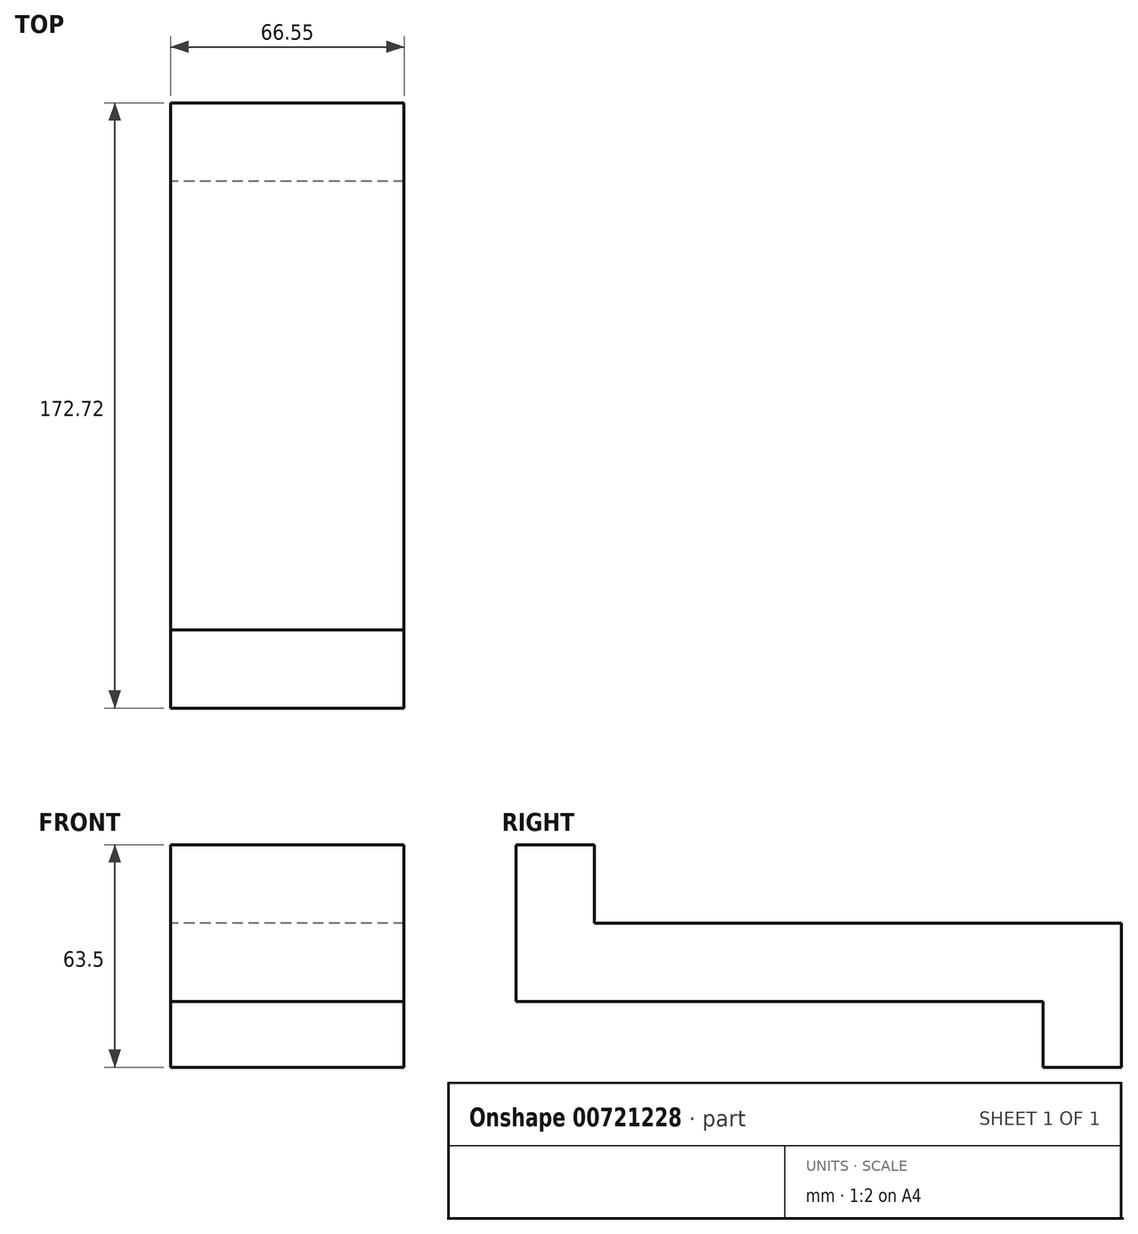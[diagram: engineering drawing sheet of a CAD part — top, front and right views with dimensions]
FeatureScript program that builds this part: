
annotation { "Feature Type Name" : "Feature", "Feature Type Description" : "" }
export const myFeature = defineFeature(function(context is Context, id is Id, definition is map)
    precondition{}
    {
        {
            var Q0;
            Q0=qCreatedBy(makeId("Right.planeOp"),FACE);
            var sketch = newSketch(context, id + "F0", { "sketchPlane" : qUnion([Q0])});
            skLineSegment(sketch, "E0.bottom", {"start": v(-92.13, 44.7) * mm, "end": v(-69.78, 44.7) * mm});
            skLineSegment(sketch, "E0.right", {"start": v(-69.78, 44.7) * mm, "end": v(-69.78, 22.35) * mm});
            skLineSegment(sketch, "E1.bottom", {"start": v(-69.78, 22.35) * mm, "end": v(80.6, 22.35) * mm});
            skLineSegment(sketch, "E1.top", {"start": v(-92.13, 0) * mm, "end": v(58.24, 0) * mm});
            skLineSegment(sketch, "E2.top", {"start": v(80.6, -18.8) * mm, "end": v(58.24, -18.8) * mm});
            skLineSegment(sketch, "E2.right", {"start": v(58.24, 0) * mm, "end": v(58.24, -18.8) * mm});
            skPoint(sketch, "E2.left.start.orphan", {"position": v(85.7, 0) * mm});
            skLineSegment(sketch, "E3", {"start": v(80.6, -18.8) * mm, "end": v(80.6, 22.35) * mm});
            skLineSegment(sketch, "E4", {"start": v(-92.13, 0) * mm, "end": v(-92.13, 44.7) * mm});
            skSolve(sketch);
        }
        {
            var Q0;
            Q0=makeQuery(id+"F0.imprint","IMPRINT",FACE,{"disambiguationData":[TD([[makeQuery(id+"F0.imprint","IMPRINT",EDGE,{"derivedFrom":sQuery(id+"F0.wireOp",EDGE,"E0.bottom")}),-1.0]])]});
            extrude(context, id + "F1", {"entities" : qUnion([Q0]), "depth" : 66.55 * mm, "offsetDistance" : 25.4 * mm});
        }
    });
